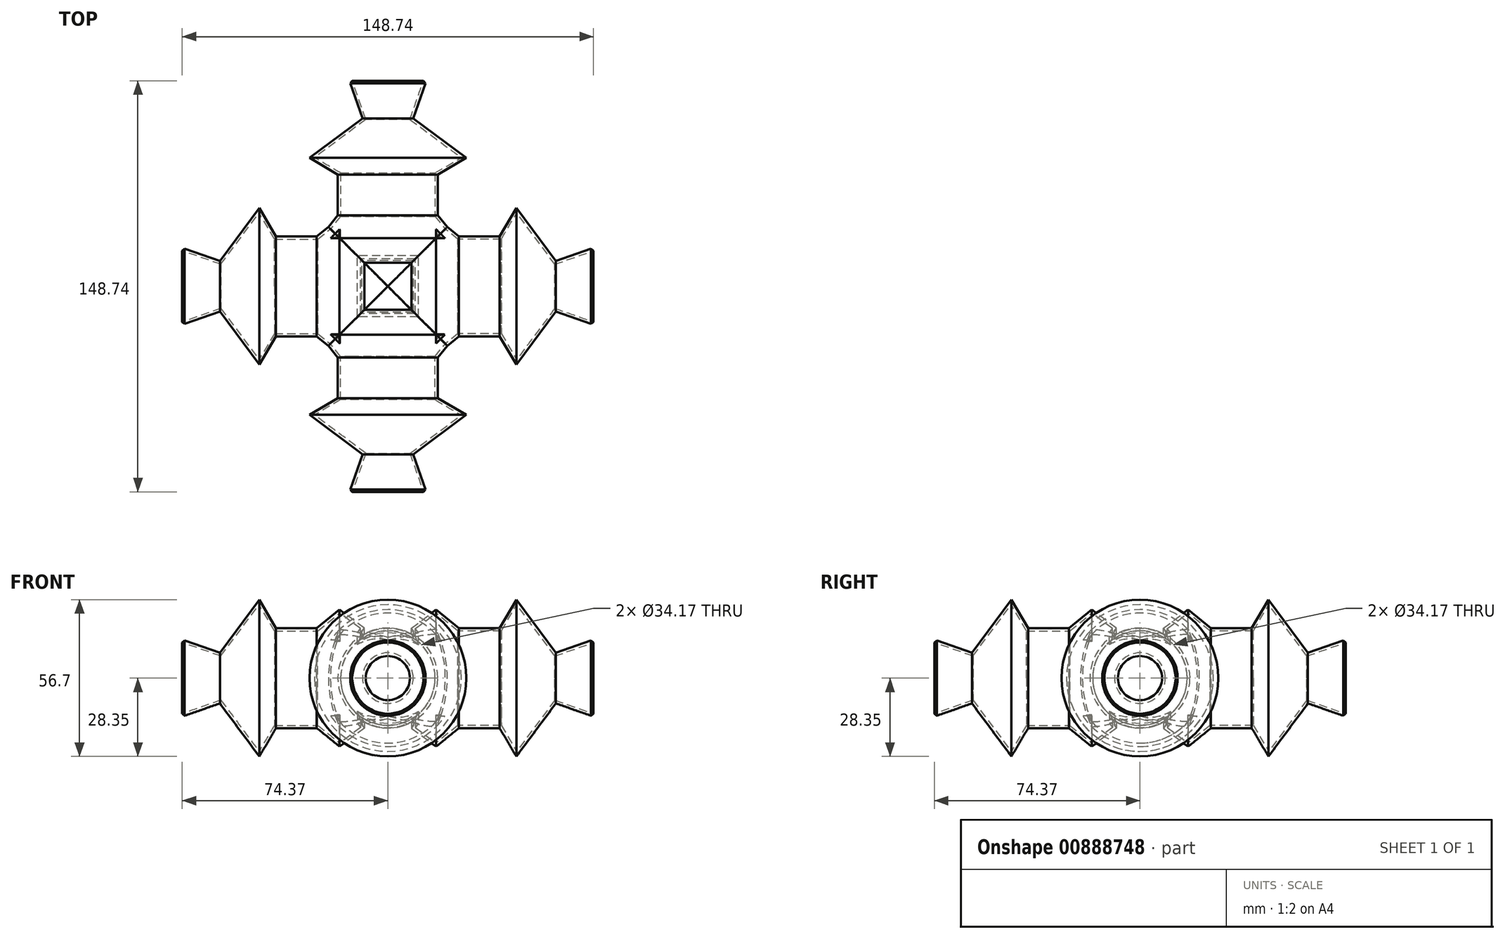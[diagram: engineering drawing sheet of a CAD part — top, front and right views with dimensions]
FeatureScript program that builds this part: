
annotation { "Feature Type Name" : "Feature", "Feature Type Description" : "" }
export const myFeature = defineFeature(function(context is Context, id is Id, definition is map)
    precondition{}
    {
        {
            var Q0;
            Q0=qCreatedBy(makeId("Top.planeOp"),FACE);
            var sketch = newSketch(context, id + "F0", { "sketchPlane" : qUnion([Q0])});
            skLineSegment(sketch, "E0", {"start": v(-90.05, 0) * mm, "end": v(-73.46, 13.62) * mm});
            skLineSegment(sketch, "E1", {"start": v(-73.46, 13.62) * mm, "end": v(-60.74, 9.16) * mm});
            skLineSegment(sketch, "E2", {"start": v(-60.74, 9.16) * mm, "end": v(-46.46, 28.35) * mm});
            skLineSegment(sketch, "E3", {"start": v(-46.46, 28.35) * mm, "end": v(-40.43, 18.08) * mm});
            skLineSegment(sketch, "E4", {"start": v(-40.43, 18.08) * mm, "end": v(-25.7, 18.08) * mm});
            skLineSegment(sketch, "E5", {"start": v(-25.7, 18.08) * mm, "end": v(-17.45, 24.78) * mm});
            skLineSegment(sketch, "E6", {"start": v(-17.45, 24.78) * mm, "end": v(-8.52, 18.08) * mm});
            skLineSegment(sketch, "E7", {"start": v(-8.52, 18.08) * mm, "end": v(-13.37, 11.62) * mm});
            skLineSegment(sketch, "E8", {"start": v(-13.37, 11.62) * mm, "end": v(14.02, 18.08) * mm});
            skLineSegment(sketch, "E9", {"start": v(14.02, 18.08) * mm, "end": v(20.5, 0) * mm});
            skLineSegment(sketch, "E10", {"start": v(20.5, 0) * mm, "end": v(-90.05, 0) * mm});
            skSolve(sketch);
        }
        {
            var Q0;
            Q0 = qSketchRegion(id + "F0", true);
            var Q1;
            Q1=sQuery(id+"F0.wireOp",EDGE,"E10");
            revolve(context, id + "F1", {"surfaceOperationType" : NewSurfaceOperationType.NEW, "entities" : qUnion([Q0]), "axis" : qUnion([Q1]), "revolveType" : RevolveType.FULL});
        }
        {
            var Q0;
            Q0=qCreatedBy(makeId("Right.planeOp"),FACE);
            var sketch = newSketch(context, id + "F2", { "sketchPlane" : qUnion([Q0])});
            skLineSegment(sketch, "E11", {"start": v(0, 37.35) * mm, "end": v(0, -44.67) * mm});
            skSolve(sketch);
        }
        {
            var Q0;
            Q0=makeQuery(id+"F1.opRevolve","SWEPT_BODY",BODY,{"disambiguationData":[OSD([sQuery(id+"F0.wireOp",EDGE,"E0"),sQuery(id+"F0.wireOp",EDGE,"E1"),sQuery(id+"F0.wireOp",EDGE,"E2"),sQuery(id+"F0.wireOp",EDGE,"E3"),sQuery(id+"F0.wireOp",EDGE,"E4"),sQuery(id+"F0.wireOp",EDGE,"E5"),sQuery(id+"F0.wireOp",EDGE,"E6"),sQuery(id+"F0.wireOp",EDGE,"E7"),sQuery(id+"F0.wireOp",EDGE,"E8"),sQuery(id+"F0.wireOp",EDGE,"E9"),sQuery(id+"F0.wireOp",EDGE,"E10")])]});
            var Q1;
            Q1=sQuery(id+"F2.wireOp",EDGE,"E11");
            circularPattern(context, id + "F3", {"operationType" : NewBodyOperationType.ADD, "entities" : qUnion([Q0]), "axis" : qUnion([Q1]), "angle" : 360 * degree, "instanceCount" : 4, "equalSpace" : true});
        }
        {
            var Q0;
            Q0=makeQuery(id+"F1.opRevolve","SWEPT_FACE",FACE,{"disambiguationData":[OSD([sQuery(id+"F0.wireOp",EDGE,"E0")])]});
            var Q1;
            Q1=makeQuery(id+"F3.opPattern","COPY",FACE,{"derivedFrom":makeQuery(id+"F1.opRevolve","SWEPT_FACE",FACE,{"disambiguationData":[OSD([sQuery(id+"F0.wireOp",EDGE,"E0")])]}),"instanceName":"3"});
            var Q2;
            Q2=makeQuery(id+"F3.opPattern","COPY",FACE,{"derivedFrom":makeQuery(id+"F1.opRevolve","SWEPT_FACE",FACE,{"disambiguationData":[OSD([sQuery(id+"F0.wireOp",EDGE,"E0")])]}),"instanceName":"2"});
            var Q3;
            Q3=makeQuery(id+"F3.opPattern","COPY",FACE,{"derivedFrom":makeQuery(id+"F1.opRevolve","SWEPT_FACE",FACE,{"disambiguationData":[OSD([sQuery(id+"F0.wireOp",EDGE,"E0")])]}),"instanceName":"1"});
            shell(context, id + "F4", {"entities" : qUnion([Q0, Q1, Q2, Q3]), "thickness" : 1 * mm});
        }
    });
